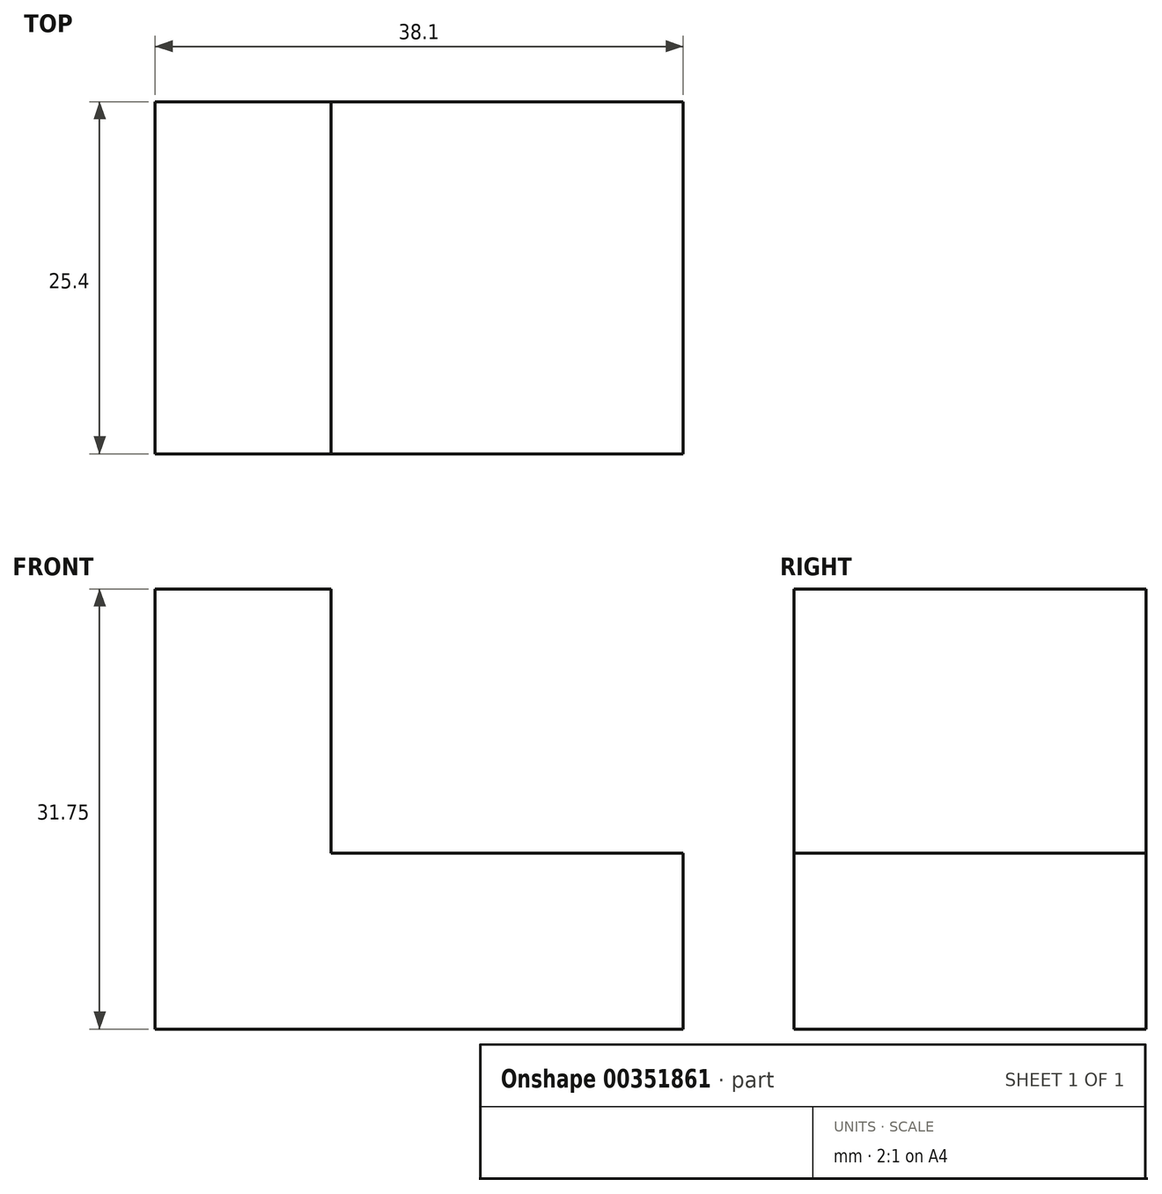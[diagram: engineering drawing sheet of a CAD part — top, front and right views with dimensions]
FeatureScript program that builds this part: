
annotation { "Feature Type Name" : "Feature", "Feature Type Description" : "" }
export const myFeature = defineFeature(function(context is Context, id is Id, definition is map)
    precondition{}
    {
        {
            var Q0;
            Q0=qCreatedBy(makeId("Front.planeOp"),FACE);
            var sketch = newSketch(context, id + "F0", { "sketchPlane" : qUnion([Q0])});
            skLineSegment(sketch, "E0", {"start": v(0, 0) * mm, "end": v(38.1, 0) * mm});
            skLineSegment(sketch, "E1", {"start": v(38.1, 12.7) * mm, "end": v(12.7, 12.7) * mm});
            skLineSegment(sketch, "E2", {"start": v(12.7, 12.7) * mm, "end": v(12.7, 31.75) * mm});
            skLineSegment(sketch, "E3", {"start": v(12.7, 31.75) * mm, "end": v(0, 31.75) * mm});
            skLineSegment(sketch, "E4", {"start": v(0, 31.75) * mm, "end": v(0, 0) * mm});
            skLineSegment(sketch, "E5", {"start": v(38.1, 0) * mm, "end": v(38.1, 12.7) * mm});
            skSolve(sketch);
        }
        {
            var Q0;
            Q0=qCreatedBy(makeId("Front.planeOp"),FACE);
            var sketch = newSketch(context, id + "F1", { "sketchPlane" : qUnion([Q0])});
            skSolve(sketch);
        }
        {
            var Q0;
            Q0 = qSketchRegion(id + "F1", true);
            var Q1;
            Q1 = qSketchRegion(id + "F0", true);
            extrude(context, id + "F2", {"entities" : qUnion([Q0, Q1]), "depth" : 25.4 * mm});
        }
    });
